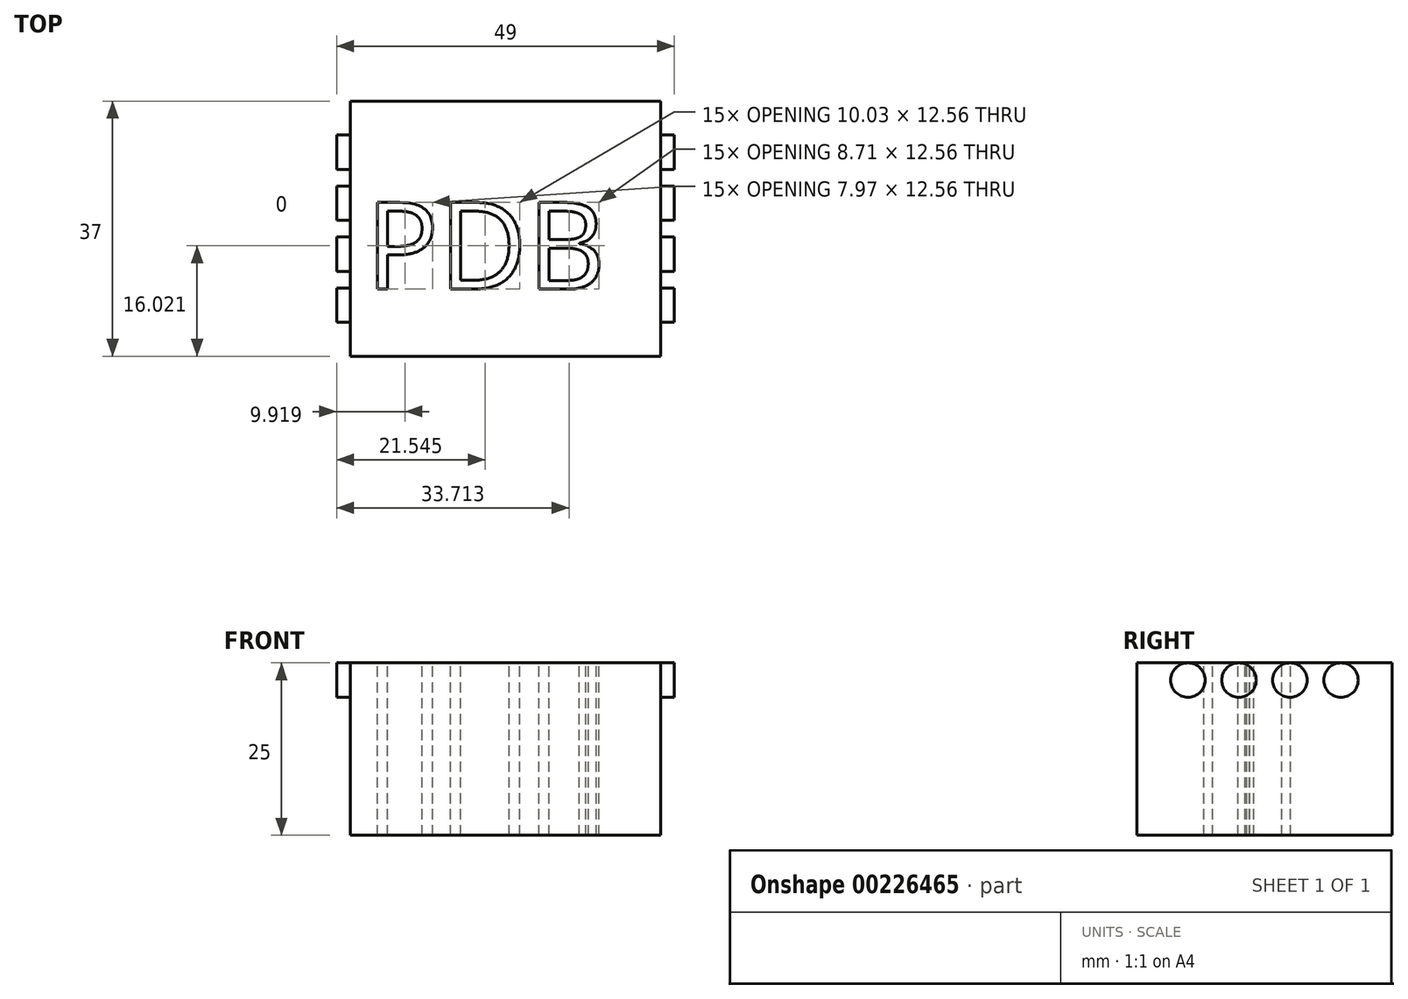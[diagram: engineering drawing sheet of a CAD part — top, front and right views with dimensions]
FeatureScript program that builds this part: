
annotation { "Feature Type Name" : "Feature", "Feature Type Description" : "" }
export const myFeature = defineFeature(function(context is Context, id is Id, definition is map)
    precondition{}
    {
        {
            var Q0;
            Q0=qCreatedBy(makeId("Top.planeOp"),FACE);
            var sketch = newSketch(context, id + "F0", { "sketchPlane" : qUnion([Q0])});
            skLineSegment(sketch, "E0.bottom", {"start": v(22.5, 18.5) * mm, "end": v(-22.5, 18.5) * mm});
            skLineSegment(sketch, "E0.top", {"start": v(22.5, -18.5) * mm, "end": v(-22.5, -18.5) * mm});
            skLineSegment(sketch, "E0.left", {"start": v(22.5, 18.5) * mm, "end": v(22.5, -18.5) * mm});
            skLineSegment(sketch, "E0.right", {"start": v(-22.5, 18.5) * mm, "end": v(-22.5, -18.5) * mm});
            skPoint(sketch, "E0.middle", {"position": v(0, 0) * mm});
            skSolve(sketch);
        }
        {
            var Q0;
            Q0=makeQuery(id+"F0.imprint","IMPRINT",FACE,{"disambiguationData":[TD([[makeQuery(id+"F0.imprint","IMPRINT",EDGE,{"derivedFrom":sQuery(id+"F0.wireOp",EDGE,"E0.bottom")}),1.0]])]});
            extrude(context, id + "F1", {"entities" : qUnion([Q0]), "depth" : 25 * mm});
        }
        {
            var Q0;
            Q0=makeQuery(id+"F1.opExtrude","SWEPT_FACE",FACE,{"disambiguationData":[OSD([sQuery(id+"F0.wireOp",EDGE,"E0.right")])]});
            var sketch = newSketch(context, id + "F2", { "sketchPlane" : qUnion([Q0])});
            skCircle(sketch, "E1", {"center": v(-11.1, 22.5) * mm, "radius": 2.5 * mm});
            skCircle(sketch, "E2", {"center": v(-3.7, 22.5) * mm, "radius": 2.5 * mm});
            skCircle(sketch, "E3", {"center": v(3.7, 22.5) * mm, "radius": 2.5 * mm});
            skCircle(sketch, "E4", {"center": v(11.1, 22.5) * mm, "radius": 2.5 * mm});
            skLineSegment(sketch, "E5", {"start": v(-18.5, 22.5) * mm, "end": v(-11.1, 22.5) * mm});
            skLineSegment(sketch, "E6", {"start": v(-3.7, 22.5) * mm, "end": v(-11.1, 22.5) * mm});
            skLineSegment(sketch, "E7", {"start": v(3.7, 22.5) * mm, "end": v(-3.7, 22.5) * mm});
            skLineSegment(sketch, "E8", {"start": v(3.7, 22.5) * mm, "end": v(11.1, 22.5) * mm});
            skLineSegment(sketch, "E9", {"start": v(11.1, 22.5) * mm, "end": v(18.5, 22.5) * mm});
            skSolve(sketch);
        }
        {
            var Q0;
            {var subQ0=sQuery(id+"F2.wireOp",EDGE,"E5");var subQ1=sQuery(id+"F2.wireOp",EDGE,"E1");var subQ2=makeQuery(id+"F2.imprint","INTERSECT",VERTEX,{"derivedFrom":[subQ1,subQ0]});Q0=makeQuery(id+"F2.imprint","IMPRINT",FACE,{"disambiguationData":[TD([[makeQuery(id+"F2.imprint","IMPRINT",EDGE,{"disambiguationData":[TD([[subQ2,1.0]])],"derivedFrom":subQ1}),1.0]])]});}
            var Q1;
            {var subQ0=sQuery(id+"F2.wireOp",EDGE,"E5");var subQ1=sQuery(id+"F2.wireOp",EDGE,"E1");var subQ2=makeQuery(id+"F2.imprint","INTERSECT",VERTEX,{"derivedFrom":[subQ1,subQ0]});Q1=makeQuery(id+"F2.imprint","IMPRINT",FACE,{"disambiguationData":[TD([[makeQuery(id+"F2.imprint","IMPRINT",EDGE,{"disambiguationData":[TD([[subQ2,-1.0]])],"derivedFrom":subQ1}),1.0]])]});}
            var Q2;
            {var subQ0=sQuery(id+"F2.wireOp",EDGE,"E6");var subQ1=sQuery(id+"F2.wireOp",EDGE,"E2");var subQ2=makeQuery(id+"F2.imprint","INTERSECT",VERTEX,{"derivedFrom":[subQ1,subQ0]});Q2=makeQuery(id+"F2.imprint","IMPRINT",FACE,{"disambiguationData":[TD([[makeQuery(id+"F2.imprint","IMPRINT",EDGE,{"disambiguationData":[TD([[subQ2,-1.0]])],"derivedFrom":subQ1}),1.0]])]});}
            var Q3;
            {var subQ0=sQuery(id+"F2.wireOp",EDGE,"E8");var subQ1=sQuery(id+"F2.wireOp",EDGE,"E3");var subQ2=makeQuery(id+"F2.imprint","INTERSECT",VERTEX,{"derivedFrom":[subQ1,subQ0]});Q3=makeQuery(id+"F2.imprint","IMPRINT",FACE,{"disambiguationData":[TD([[makeQuery(id+"F2.imprint","IMPRINT",EDGE,{"disambiguationData":[TD([[subQ2,-1.0]])],"derivedFrom":subQ1}),1.0]])]});}
            var Q4;
            {var subQ0=sQuery(id+"F2.wireOp",EDGE,"E9");var subQ1=sQuery(id+"F2.wireOp",EDGE,"E4");var subQ2=makeQuery(id+"F2.imprint","INTERSECT",VERTEX,{"derivedFrom":[subQ1,subQ0]});Q4=makeQuery(id+"F2.imprint","IMPRINT",FACE,{"disambiguationData":[TD([[makeQuery(id+"F2.imprint","IMPRINT",EDGE,{"disambiguationData":[TD([[subQ2,-1.0]])],"derivedFrom":subQ1}),1.0]])]});}
            var Q5;
            {var subQ0=sQuery(id+"F2.wireOp",EDGE,"E9");var subQ1=sQuery(id+"F2.wireOp",EDGE,"E4");var subQ2=makeQuery(id+"F2.imprint","INTERSECT",VERTEX,{"derivedFrom":[subQ1,subQ0]});Q5=makeQuery(id+"F2.imprint","IMPRINT",FACE,{"disambiguationData":[TD([[makeQuery(id+"F2.imprint","IMPRINT",EDGE,{"disambiguationData":[TD([[subQ2,1.0]])],"derivedFrom":subQ1}),1.0]])]});}
            var Q6;
            {var subQ0=sQuery(id+"F2.wireOp",EDGE,"E8");var subQ1=sQuery(id+"F2.wireOp",EDGE,"E3");var subQ2=makeQuery(id+"F2.imprint","INTERSECT",VERTEX,{"derivedFrom":[subQ1,subQ0]});Q6=makeQuery(id+"F2.imprint","IMPRINT",FACE,{"disambiguationData":[TD([[makeQuery(id+"F2.imprint","IMPRINT",EDGE,{"disambiguationData":[TD([[subQ2,1.0]])],"derivedFrom":subQ1}),1.0]])]});}
            var Q7;
            {var subQ0=sQuery(id+"F2.wireOp",EDGE,"E6");var subQ1=sQuery(id+"F2.wireOp",EDGE,"E2");var subQ2=makeQuery(id+"F2.imprint","INTERSECT",VERTEX,{"derivedFrom":[subQ1,subQ0]});Q7=makeQuery(id+"F2.imprint","IMPRINT",FACE,{"disambiguationData":[TD([[makeQuery(id+"F2.imprint","IMPRINT",EDGE,{"disambiguationData":[TD([[subQ2,1.0]])],"derivedFrom":subQ1}),1.0]])]});}
            extrude(context, id + "F3", {"entities" : qUnion([Q0, Q1, Q2, Q3, Q4, Q5, Q6, Q7]), "depth" : 2 * mm});
        }
        {
            var Q0;
            Q0=makeQuery(id+"F1.opExtrude","SWEPT_FACE",FACE,{"disambiguationData":[OSD([sQuery(id+"F0.wireOp",EDGE,"E0.left")])]});
            var sketch = newSketch(context, id + "F4", { "sketchPlane" : qUnion([Q0])});
            skCircle(sketch, "E10", {"center": v(-11.1, 22.5) * mm, "radius": 2.5 * mm});
            skCircle(sketch, "E11", {"center": v(-3.7, 22.5) * mm, "radius": 2.5 * mm});
            skCircle(sketch, "E12", {"center": v(3.7, 22.5) * mm, "radius": 2.5 * mm});
            skCircle(sketch, "E13", {"center": v(11.1, 22.5) * mm, "radius": 2.5 * mm});
            skLineSegment(sketch, "E14", {"start": v(-18.5, 22.5) * mm, "end": v(-11.1, 22.5) * mm});
            skLineSegment(sketch, "E15", {"start": v(-11.1, 22.5) * mm, "end": v(-3.7, 22.5) * mm});
            skLineSegment(sketch, "E16", {"start": v(3.7, 22.5) * mm, "end": v(-3.7, 22.5) * mm});
            skLineSegment(sketch, "E17", {"start": v(3.7, 22.5) * mm, "end": v(11.1, 22.5) * mm});
            skLineSegment(sketch, "E18", {"start": v(11.1, 22.5) * mm, "end": v(18.5, 22.5) * mm});
            skSolve(sketch);
        }
        {
            var Q0;
            {var subQ0=sQuery(id+"F4.wireOp",EDGE,"E14");var subQ1=sQuery(id+"F4.wireOp",EDGE,"E10");var subQ2=makeQuery(id+"F4.imprint","INTERSECT",VERTEX,{"derivedFrom":[subQ1,subQ0]});Q0=makeQuery(id+"F4.imprint","IMPRINT",FACE,{"disambiguationData":[TD([[makeQuery(id+"F4.imprint","IMPRINT",EDGE,{"disambiguationData":[TD([[subQ2,1.0]])],"derivedFrom":subQ1}),1.0]])]});}
            var Q1;
            {var subQ0=sQuery(id+"F4.wireOp",EDGE,"E14");var subQ1=sQuery(id+"F4.wireOp",EDGE,"E10");var subQ2=makeQuery(id+"F4.imprint","INTERSECT",VERTEX,{"derivedFrom":[subQ1,subQ0]});Q1=makeQuery(id+"F4.imprint","IMPRINT",FACE,{"disambiguationData":[TD([[makeQuery(id+"F4.imprint","IMPRINT",EDGE,{"disambiguationData":[TD([[subQ2,-1.0]])],"derivedFrom":subQ1}),1.0]])]});}
            var Q2;
            {var subQ0=sQuery(id+"F4.wireOp",EDGE,"E15");var subQ1=sQuery(id+"F4.wireOp",EDGE,"E11");var subQ2=makeQuery(id+"F4.imprint","INTERSECT",VERTEX,{"derivedFrom":[subQ1,subQ0]});Q2=makeQuery(id+"F4.imprint","IMPRINT",FACE,{"disambiguationData":[TD([[makeQuery(id+"F4.imprint","IMPRINT",EDGE,{"disambiguationData":[TD([[subQ2,1.0]])],"derivedFrom":subQ1}),1.0]])]});}
            var Q3;
            {var subQ0=sQuery(id+"F4.wireOp",EDGE,"E15");var subQ1=sQuery(id+"F4.wireOp",EDGE,"E11");var subQ2=makeQuery(id+"F4.imprint","INTERSECT",VERTEX,{"derivedFrom":[subQ1,subQ0]});Q3=makeQuery(id+"F4.imprint","IMPRINT",FACE,{"disambiguationData":[TD([[makeQuery(id+"F4.imprint","IMPRINT",EDGE,{"disambiguationData":[TD([[subQ2,-1.0]])],"derivedFrom":subQ1}),1.0]])]});}
            var Q4;
            {var subQ0=sQuery(id+"F4.wireOp",EDGE,"E15");var subQ1=sQuery(id+"F4.wireOp",EDGE,"E11");var subQ2=makeQuery(id+"F4.imprint","INTERSECT",VERTEX,{"derivedFrom":[subQ1,subQ0]});Q4=makeQuery(id+"F4.imprint","IMPRINT",FACE,{"disambiguationData":[TD([[makeQuery(id+"F4.imprint","IMPRINT",EDGE,{"disambiguationData":[TD([[subQ2,-1.0]])],"derivedFrom":subQ1}),1.0]])]});}
            var Q5;
            {var subQ0=sQuery(id+"F4.wireOp",EDGE,"E16");var subQ1=sQuery(id+"F4.wireOp",EDGE,"E12");var subQ2=makeQuery(id+"F4.imprint","INTERSECT",VERTEX,{"derivedFrom":[subQ1,subQ0]});Q5=makeQuery(id+"F4.imprint","IMPRINT",FACE,{"disambiguationData":[TD([[makeQuery(id+"F4.imprint","IMPRINT",EDGE,{"disambiguationData":[TD([[subQ2,1.0]])],"derivedFrom":subQ1}),1.0]])]});}
            var Q6;
            {var subQ0=sQuery(id+"F4.wireOp",EDGE,"E16");var subQ1=sQuery(id+"F4.wireOp",EDGE,"E12");var subQ2=makeQuery(id+"F4.imprint","INTERSECT",VERTEX,{"derivedFrom":[subQ1,subQ0]});Q6=makeQuery(id+"F4.imprint","IMPRINT",FACE,{"disambiguationData":[TD([[makeQuery(id+"F4.imprint","IMPRINT",EDGE,{"disambiguationData":[TD([[subQ2,-1.0]])],"derivedFrom":subQ1}),1.0]])]});}
            var Q7;
            {var subQ0=sQuery(id+"F4.wireOp",EDGE,"E18");var subQ1=sQuery(id+"F4.wireOp",EDGE,"E13");var subQ2=makeQuery(id+"F4.imprint","INTERSECT",VERTEX,{"derivedFrom":[subQ1,subQ0]});Q7=makeQuery(id+"F4.imprint","IMPRINT",FACE,{"disambiguationData":[TD([[makeQuery(id+"F4.imprint","IMPRINT",EDGE,{"disambiguationData":[TD([[subQ2,-1.0]])],"derivedFrom":subQ1}),1.0]])]});}
            var Q8;
            {var subQ0=sQuery(id+"F4.wireOp",EDGE,"E18");var subQ1=sQuery(id+"F4.wireOp",EDGE,"E13");var subQ2=makeQuery(id+"F4.imprint","INTERSECT",VERTEX,{"derivedFrom":[subQ1,subQ0]});Q8=makeQuery(id+"F4.imprint","IMPRINT",FACE,{"disambiguationData":[TD([[makeQuery(id+"F4.imprint","IMPRINT",EDGE,{"disambiguationData":[TD([[subQ2,1.0]])],"derivedFrom":subQ1}),1.0]])]});}
            extrude(context, id + "F5", {"entities" : qUnion([Q0, Q1, Q2, Q3, Q4, Q5, Q6, Q7, Q8]), "depth" : 2 * mm});
        }
        {
            var Q0;
            Q0=makeQuery(id+"F1.opExtrude","CAP_FACE",FACE,{"disambiguationData":[OSD([sQuery(id+"F0.wireOp",EDGE,"E0.bottom"),sQuery(id+"F0.wireOp",EDGE,"E0.top"),sQuery(id+"F0.wireOp",EDGE,"E0.left"),sQuery(id+"F0.wireOp",EDGE,"E0.right")])],"isStart":false});
            var sketch = newSketch(context, id + "F6", { "sketchPlane" : qUnion([Q0])});
            skText(sketch, "E19", { "text": "PDB", "fontName": "OpenSans-Regular.ttf"});
            const initialGuessF6  = {"E19": [-0.02029, -0.00876, 1, 0, 0.01267]};
            skSetInitialGuess(sketch, initialGuessF6);
            skSolve(sketch);
        }
        {
            var Q0;
            Q0 = qSketchRegion(id + "F6", true);
            extrude(context, id + "F7", {"entities" : qUnion([Q0]), "operationType" : NewBodyOperationType.REMOVE, "oppositeDirection" : true, "depth" : 25.4 * mm});
        }
    });
